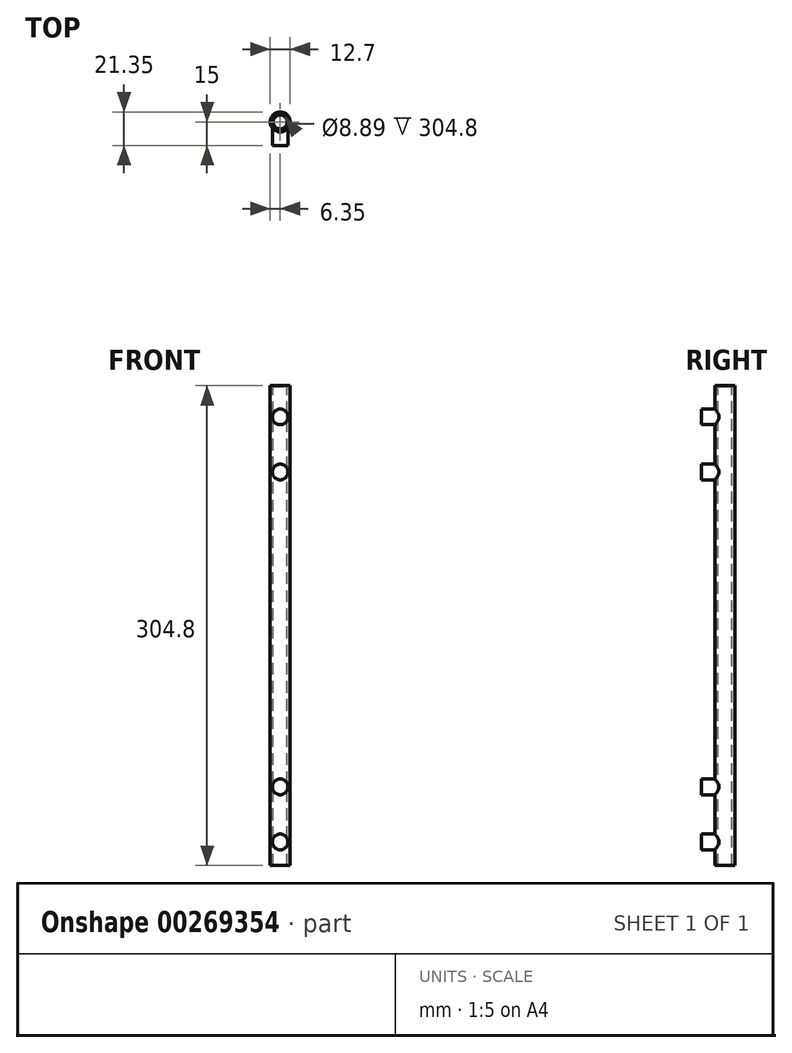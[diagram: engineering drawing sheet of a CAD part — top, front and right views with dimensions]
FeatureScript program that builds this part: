
annotation { "Feature Type Name" : "Feature", "Feature Type Description" : "" }
export const myFeature = defineFeature(function(context is Context, id is Id, definition is map)
    precondition{}
    {
        {
            var Q0;
            Q0=qCreatedBy(makeId("Top.planeOp"),FACE);
            var sketch = newSketch(context, id + "F0", { "sketchPlane" : qUnion([Q0])});
            skCircle(sketch, "E0", {"center": v(0, 0) * mm, "radius": 6.35 * mm});
            skSolve(sketch);
        }
        {
            var Q0;
            Q0=makeQuery(id+"F0.imprint","IMPRINT",FACE,{"disambiguationData":[TD([[makeQuery(id+"F0.imprint","IMPRINT",EDGE,{"derivedFrom":sQuery(id+"F0.wireOp",EDGE,"E0")}),1.0]])]});
            extrude(context, id + "F1", {"entities" : qUnion([Q0]), "depth" : 304.8 * mm});
        }
        {
            var Q0;
            Q0=qCreatedBy(makeId("Front.planeOp"),FACE);
            var sketch = newSketch(context, id + "F2", { "sketchPlane" : qUnion([Q0])});
            skCircle(sketch, "E1", {"center": v(0, 15) * mm, "radius": 5 * mm});
            skCircle(sketch, "E2", {"center": v(0, 50) * mm, "radius": 5 * mm});
            skCircle(sketch, "E3", {"center": v(0, 250) * mm, "radius": 5 * mm});
            skCircle(sketch, "E4", {"center": v(0, 285) * mm, "radius": 5 * mm});
            skSolve(sketch);
        }
        {
            var Q0;
            Q0=makeQuery(id+"F1.opExtrude","CAP_FACE",FACE,{"disambiguationData":[OSD([sQuery(id+"F0.wireOp",EDGE,"E0")])],"isStart":false});
            var sketch = newSketch(context, id + "F3", { "sketchPlane" : qUnion([Q0])});
            skCircle(sketch, "E5", {"center": v(0, 0) * mm, "radius": 4.45 * mm});
            skSolve(sketch);
        }
        {
            var Q0;
            Q0 = qSketchRegion(id + "F2", true);
            extrude(context, id + "F4", {"entities" : qUnion([Q0]), "operationType" : NewBodyOperationType.ADD, "depth" : 15 * mm});
        }
        {
            var Q0;
            Q0 = qSketchRegion(id + "F3", true);
            extrude(context, id + "F5", {"entities" : qUnion([Q0]), "operationType" : NewBodyOperationType.REMOVE, "endBound" : BoundingType.THROUGH_ALL, "oppositeDirection" : true, "depth" : 295 * mm});
        }
        {
            var Q0;
            Q0=makeQuery(id+"F1.opExtrude","CAP_FACE",FACE,{"disambiguationData":[OSD([sQuery(id+"F0.wireOp",EDGE,"E0")])],"isStart":false});
            var sketch = newSketch(context, id + "F6", { "sketchPlane" : qUnion([Q0])});
            skCircle(sketch, "E6", {"center": v(0, 0) * mm, "radius": 5.46 * mm});
            skSolve(sketch);
        }
        {
            var Q0;
            Q0=qCreatedBy(makeId("Front.planeOp"),FACE);
            var sketch = newSketch(context, id + "F7", { "sketchPlane" : qUnion([Q0])});
            skArc(sketch, "E7", {"start": v(-6, 304.8) * mm, "mid": v(-5.5, 304.3) * mm, "end": v(-5, 304.8) * mm});
            skLineSegment(sketch, "E8", {"start": v(-5, 304.8) * mm, "end": v(-6, 304.8) * mm});
            skSolve(sketch);
        }
        {
            var Q0;
            Q0 = qSketchRegion(id + "F7", true);
            var Q1;
            Q1 = qConstructionFilter(qBodyType(qCreatedBy(id + "F6" ,EDGE), BodyType.WIRE), ConstructionObject.NO);
            sweep(context, id + "F8", {"operationType" : NewBodyOperationType.REMOVE, "profiles" : qUnion([Q0]), "path" : qUnion([Q1])});
        }
        {
            var Q0;
            Q0=qCreatedBy(makeId("Top.planeOp"),FACE);
            cPlane(context, id + "F9", {"entities" : qUnion([Q0]), "cplaneType" : CPlaneType.OFFSET, "offset" : 152.4 * mm, "width" : 150 * mm, "height" : 150 * mm});
        }
    });
